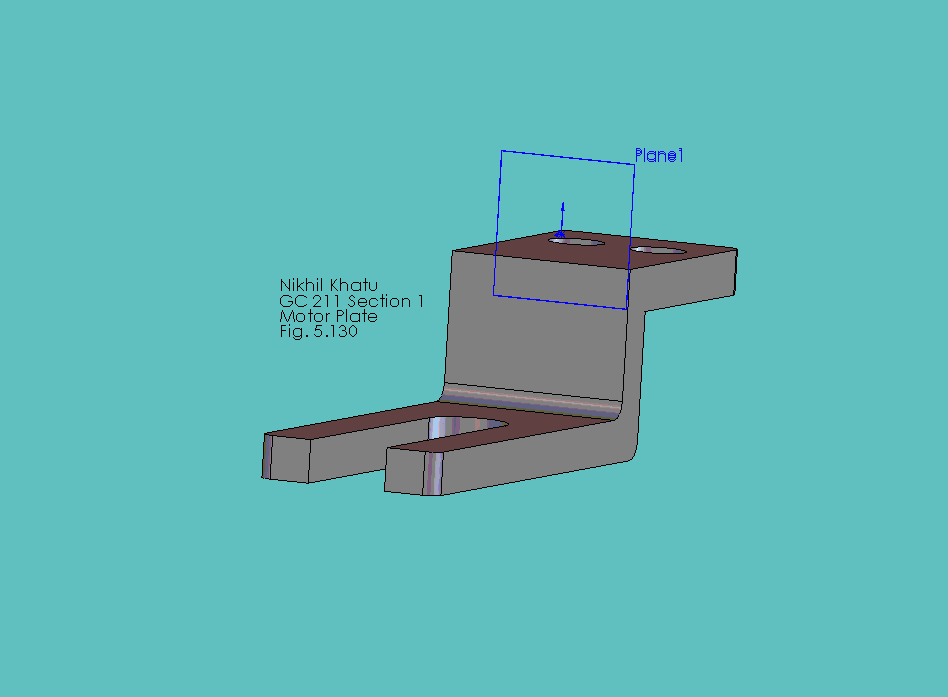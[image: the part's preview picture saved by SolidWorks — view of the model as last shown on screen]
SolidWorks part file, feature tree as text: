
SOLIDWORKS PART (.sldprt)
format: sldprt  version: not decoded by parser v0  size: 307,200 bytes
history: native  units: mm
features: sketch x5, plane x4, cut_extrude x4, fillet x3, material x1, extrude x1 (+11 scaffold rows collapsed)
feature tree (29):
  scaffold x11  (default folders/planes/origin — collapsed)
  material  "Ductile Iron"
  plane  "Frontal"
  plane  "Horizontal"
  plane  "Profile"
  sketch  "Sketch1"  dims[D1=6710.68mm D2=1778.0mm]
  extrude  "Extrude1"  Depth=1778mm
  sketch  "Sketch2"  dims[c1.D1=2540.0mm c1.D2=~1360.567295mm c2.D1=2138.68mm c2.D2=1376.68mm]
  cut_extrude  "Cut-Extrude3"  [1 undecoded]
  plane  "Plane1"
  sketch  "Sketch6"  dims[D1=1376.68mm D2=4170.68mm]
  cut_extrude  "Cut-Extrude4"  [1 undecoded]
  sketch  "Sketch8"  dims[D1=508.0mm D2=2692.4mm]
  cut_extrude  "Cut-Extrude5"  [1 undecoded]
  sketch  "Sketch9"  dims[c1.D3=523.24mm c1.D1=1727.2mm c1.D2=812.8mm c2.D3=482.6mm]
  cut_extrude  "Cut-Extrude6"  [1 undecoded]
  fillet  "Fillet2"  Radius=162.56mm
  fillet  "Fillet3"  Radius=162.56mm
  fillet  "Fillet4"  Radius=127mm
decode coverage: 9 of 13 modeling features carry decoded parameters
note: ~ marks probable driven/reference dimensions
note: 4 parameter values undecoded
summary: no parameter record found for 4 features
note: suppression state not decoded; provenance and decode notes live in map.json
